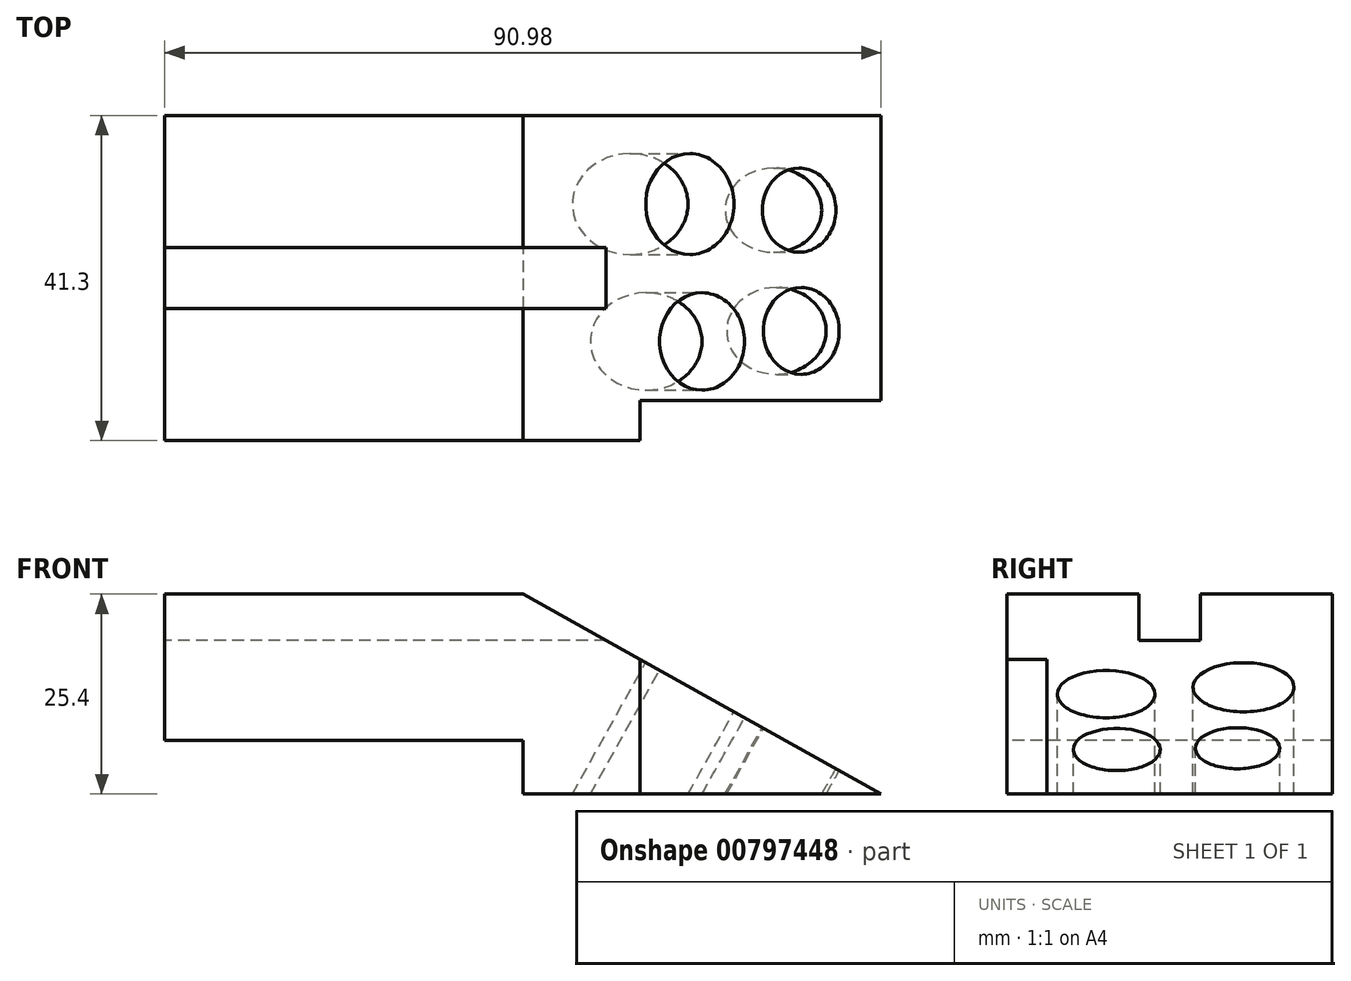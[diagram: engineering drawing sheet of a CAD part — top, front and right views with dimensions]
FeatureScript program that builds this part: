
annotation { "Feature Type Name" : "Feature", "Feature Type Description" : "" }
export const myFeature = defineFeature(function(context is Context, id is Id, definition is map)
    precondition{}
    {
        {
            var Q0;
            Q0=qCreatedBy(makeId("Top.planeOp"),FACE);
            var sketch = newSketch(context, id + "F0", { "sketchPlane" : qUnion([Q0])});
            skLineSegment(sketch, "E0.bottom", {"start": v(45.5, 20.65) * mm, "end": v(-45.5, 20.65) * mm});
            skLineSegment(sketch, "E0.top", {"start": v(45.5, -20.65) * mm, "end": v(-45.5, -20.65) * mm});
            skLineSegment(sketch, "E0.left", {"start": v(45.5, 20.65) * mm, "end": v(45.5, -20.65) * mm});
            skLineSegment(sketch, "E0.right", {"start": v(-45.5, 20.65) * mm, "end": v(-45.5, -20.65) * mm});
            skPoint(sketch, "E0.middle", {"position": v(0, 0) * mm});
            skSolve(sketch);
        }
        {
            var Q0;
            Q0=makeQuery(id+"F0.imprint","IMPRINT",FACE,{"disambiguationData":[TD([[makeQuery(id+"F0.imprint","IMPRINT",EDGE,{"derivedFrom":sQuery(id+"F0.wireOp",EDGE,"E0.bottom")}),1.0]])]});
            extrude(context, id + "F1", {"entities" : qUnion([Q0]), "depth" : 25.4 * mm, "offsetDistance" : 25.4 * mm});
        }
        {
            var Q0;
            Q0=makeQuery(id+"F1.opExtrude","SWEPT_FACE",FACE,{"disambiguationData":[OSD([sQuery(id+"F0.wireOp",EDGE,"E0.top")])]});
            var sketch = newSketch(context, id + "F2", { "sketchPlane" : qUnion([Q0])});
            skLineSegment(sketch, "E1", {"start": v(0, 25.4) * mm, "end": v(45.5, 0) * mm});
            skLineSegment(sketch, "E2", {"start": v(45.5, 0) * mm, "end": v(58.2, 35.67) * mm});
            skLineSegment(sketch, "E3", {"start": v(58.2, 35.67) * mm, "end": v(0, 25.4) * mm});
            skSolve(sketch);
        }
        {
            var Q0;
            {var subQ0=sQuery(id+"F2.wireOp",EDGE,"E1");Q0=makeQuery(id+"F2.imprint","IMPRINT",FACE,{"disambiguationData":[TD([[makeQuery(id+"F2.imprint","IMPRINT",EDGE,{"derivedFrom":subQ0}),1.0]])]});}
            extrude(context, id + "F3", {"entities" : qUnion([Q0]), "operationType" : NewBodyOperationType.REMOVE, "oppositeDirection" : true, "depth" : 50.8 * mm, "offsetDistance" : 25.4 * mm});
        }
        {
            var Q0;
            Q0=makeQuery(id+"F1.opExtrude","SWEPT_FACE",FACE,{"disambiguationData":[OSD([sQuery(id+"F0.wireOp",EDGE,"E0.right")])]});
            var sketch = newSketch(context, id + "F4", { "sketchPlane" : qUnion([Q0])});
            skLineSegment(sketch, "E4.bottom", {"start": v(-3.9, 25.4) * mm, "end": v(3.9, 25.4) * mm});
            skLineSegment(sketch, "E4.top", {"start": v(-3.9, 19.5) * mm, "end": v(3.9, 19.5) * mm});
            skLineSegment(sketch, "E4.left", {"start": v(-3.9, 25.4) * mm, "end": v(-3.9, 19.5) * mm});
            skLineSegment(sketch, "E4.right", {"start": v(3.9, 25.4) * mm, "end": v(3.9, 19.5) * mm});
            skSolve(sketch);
        }
        {
            var Q0;
            Q0=makeQuery(id+"F4.imprint","IMPRINT",FACE,{"disambiguationData":[TD([[makeQuery(id+"F4.imprint","IMPRINT",EDGE,{"derivedFrom":sQuery(id+"F4.wireOp",EDGE,"E4.bottom")}),-1.0]])]});
            extrude(context, id + "F5", {"entities" : qUnion([Q0]), "operationType" : NewBodyOperationType.REMOVE, "oppositeDirection" : true, "depth" : 101.6 * mm, "offsetDistance" : 25.4 * mm});
        }
        {
            var Q0;
            Q0=makeQuery(id+"F3.boolean.opBoolean","COPY",FACE,{"derivedFrom":makeQuery(id+"F3.opExtrude","SWEPT_FACE",FACE,{"disambiguationData":[OSD([sQuery(id+"F2.wireOp",EDGE,"E1")])]})});
            var sketch = newSketch(context, id + "F6", { "sketchPlane" : qUnion([Q0])});
            skCircle(sketch, "E5", {"center": v(13.67, -8.05) * mm, "radius": 6.18 * mm});
            skPoint(sketch, "E5.centerSnap0", {"position": v(13.67, -20.65) * mm});
            skCircle(sketch, "E6", {"center": v(11.9, 9.4) * mm, "radius": 6.41 * mm});
            skCircle(sketch, "E7", {"center": v(27.79, 8.62) * mm, "radius": 5.35 * mm});
            skCircle(sketch, "E8", {"center": v(28.1, -6.71) * mm, "radius": 5.52 * mm});
            skSolve(sketch);
        }
        {
            var Q0;
            Q0=makeQuery(id+"F6.imprint","IMPRINT",FACE,{"disambiguationData":[TD([[makeQuery(id+"F6.imprint","IMPRINT",EDGE,{"derivedFrom":sQuery(id+"F6.wireOp",EDGE,"E5")}),1.0]])]});
            var Q1;
            Q1=makeQuery(id+"F6.imprint","IMPRINT",FACE,{"disambiguationData":[TD([[makeQuery(id+"F6.imprint","IMPRINT",EDGE,{"derivedFrom":sQuery(id+"F6.wireOp",EDGE,"E6")}),1.0]])]});
            var Q2;
            Q2=makeQuery(id+"F6.imprint","IMPRINT",FACE,{"disambiguationData":[TD([[makeQuery(id+"F6.imprint","IMPRINT",EDGE,{"derivedFrom":sQuery(id+"F6.wireOp",EDGE,"E7")}),1.0]])]});
            var Q3;
            Q3=makeQuery(id+"F6.imprint","IMPRINT",FACE,{"disambiguationData":[TD([[makeQuery(id+"F6.imprint","IMPRINT",EDGE,{"derivedFrom":sQuery(id+"F6.wireOp",EDGE,"E8")}),1.0]])]});
            extrude(context, id + "F7", {"entities" : qUnion([Q0, Q1, Q2, Q3]), "operationType" : NewBodyOperationType.REMOVE, "endBound" : BoundingType.THROUGH_ALL, "oppositeDirection" : true, "depth" : 25.4 * mm, "offsetDistance" : 25.4 * mm});
        }
        {
            var Q0;
            Q0=makeQuery(id+"F1.opExtrude","SWEPT_FACE",FACE,{"disambiguationData":[OSD([sQuery(id+"F0.wireOp",EDGE,"E0.top")])]});
            var sketch = newSketch(context, id + "F8", { "sketchPlane" : qUnion([Q0])});
            skLineSegment(sketch, "E9", {"start": v(14.88, 0) * mm, "end": v(14.88, 24.4) * mm});
            skLineSegment(sketch, "E10", {"start": v(14.88, 24.4) * mm, "end": v(45.5, 0) * mm});
            skLineSegment(sketch, "E11", {"start": v(45.5, 0) * mm, "end": v(14.88, 0) * mm});
            skSolve(sketch);
        }
        {
            var Q0;
            {var subQ0=sQuery(id+"F8.wireOp",EDGE,"E11");Q0=makeQuery(id+"F8.imprint","IMPRINT",FACE,{"disambiguationData":[TD([[makeQuery(id+"F8.imprint","IMPRINT",EDGE,{"derivedFrom":subQ0}),-1.0]])]});}
            extrude(context, id + "F9", {"entities" : qUnion([Q0]), "operationType" : NewBodyOperationType.REMOVE, "oppositeDirection" : true, "depth" : 5.08 * mm, "offsetDistance" : 25.4 * mm});
        }
        {
            var Q0;
            Q0=makeQuery(id+"F1.opExtrude","SWEPT_FACE",FACE,{"disambiguationData":[OSD([sQuery(id+"F0.wireOp",EDGE,"E0.top")])]});
            var sketch = newSketch(context, id + "F10", { "sketchPlane" : qUnion([Q0])});
            skLineSegment(sketch, "E12.bottom", {"start": v(0, 0) * mm, "end": v(-45.5, 0) * mm});
            skLineSegment(sketch, "E12.top", {"start": v(0, 6.79) * mm, "end": v(-45.5, 6.79) * mm});
            skLineSegment(sketch, "E12.left", {"start": v(0, 0) * mm, "end": v(0, 6.79) * mm});
            skLineSegment(sketch, "E12.right", {"start": v(-45.5, 0) * mm, "end": v(-45.5, 6.79) * mm});
            skSolve(sketch);
        }
        {
            var Q0;
            Q0=makeQuery(id+"F10.imprint","IMPRINT",FACE,{"disambiguationData":[TD([[makeQuery(id+"F10.imprint","IMPRINT",EDGE,{"derivedFrom":sQuery(id+"F10.wireOp",EDGE,"E12.bottom")}),-1.0]])]});
            extrude(context, id + "F11", {"entities" : qUnion([Q0]), "operationType" : NewBodyOperationType.REMOVE, "endBound" : BoundingType.THROUGH_ALL, "oppositeDirection" : true, "depth" : 25.4 * mm, "offsetDistance" : 25.4 * mm});
        }
    });
